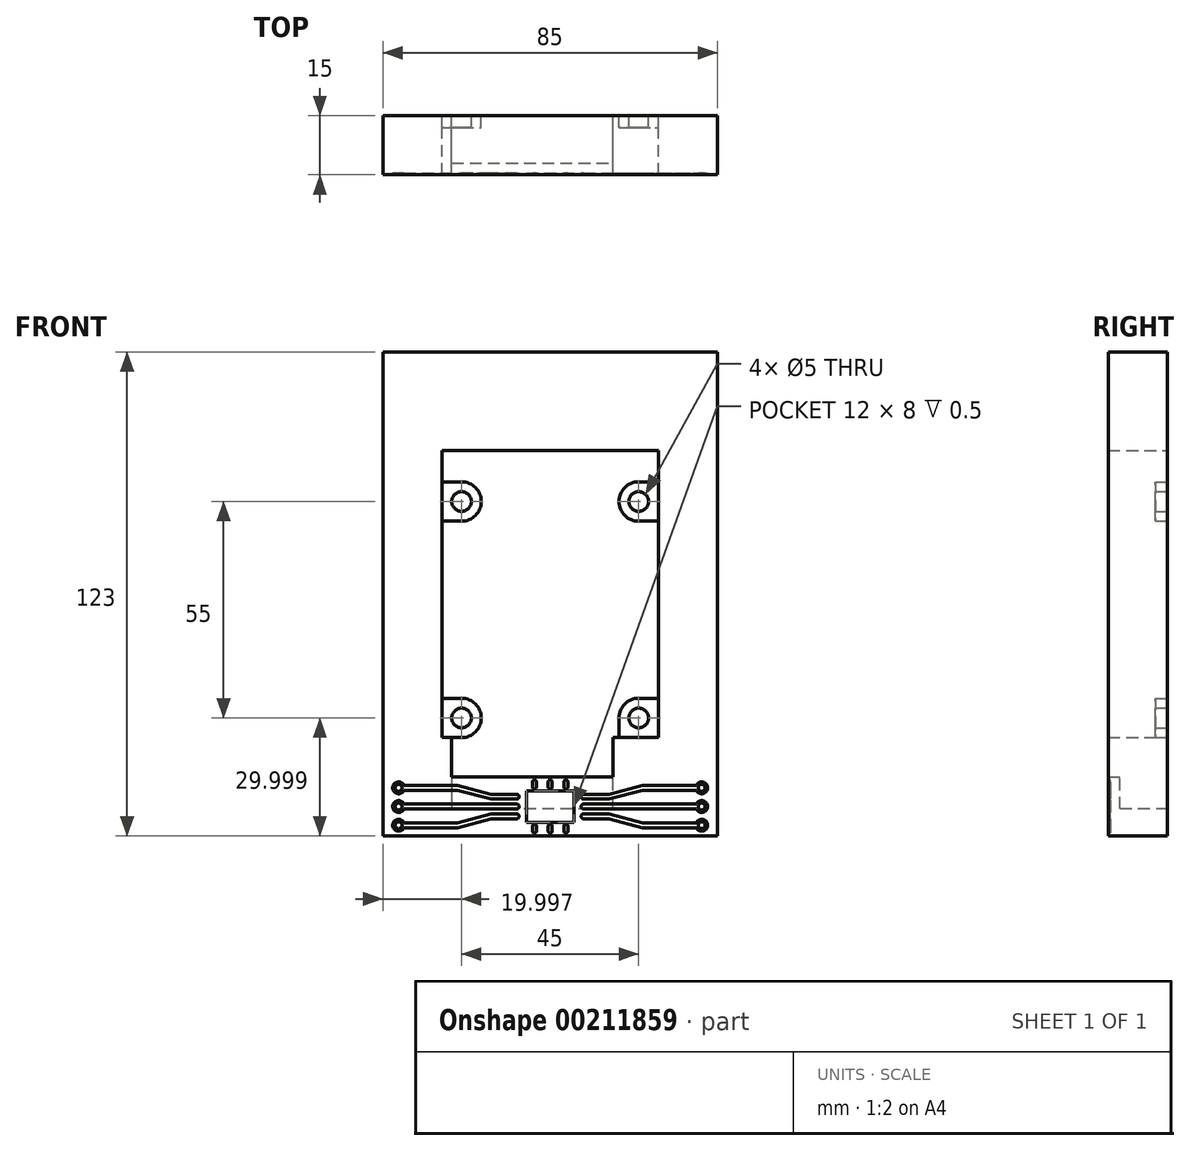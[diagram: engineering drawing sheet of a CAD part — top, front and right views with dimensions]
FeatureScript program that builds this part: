
annotation { "Feature Type Name" : "Feature", "Feature Type Description" : "" }
export const myFeature = defineFeature(function(context is Context, id is Id, definition is map)
    precondition{}
    {
        {
            var Q0;
            Q0=qCreatedBy(makeId("Front.planeOp"),FACE);
            var sketch = newSketch(context, id + "F0", { "sketchPlane" : qUnion([Q0])});
            skLineSegment(sketch, "E0.bottom", {"start": v(-49.2, 57.76) * mm, "end": v(35.8, 57.76) * mm});
            skLineSegment(sketch, "E0.top", {"start": v(-49.2, -65.24) * mm, "end": v(35.8, -65.24) * mm});
            skLineSegment(sketch, "E0.left", {"start": v(-49.2, 57.76) * mm, "end": v(-49.2, -65.24) * mm});
            skLineSegment(sketch, "E0.right", {"start": v(35.8, 57.76) * mm, "end": v(35.8, -65.24) * mm});
            skLineSegment(sketch, "E1.bottom", {"start": v(-34.2, 32.76) * mm, "end": v(20.8, 32.76) * mm});
            skLineSegment(sketch, "E1.top", {"start": v(-34.2, -40.24) * mm, "end": v(20.8, -40.24) * mm});
            skLineSegment(sketch, "E1.left", {"start": v(-34.2, 32.76) * mm, "end": v(-34.2, -40.24) * mm});
            skLineSegment(sketch, "E1.right", {"start": v(20.8, 32.76) * mm, "end": v(20.8, -40.24) * mm});
            skLineSegment(sketch, "E2", {"start": v(-34.2, 21.12) * mm, "end": v(-49.2, 21.12) * mm, "construction": true});
            skLineSegment(sketch, "E3", {"start": v(20.8, 21.67) * mm, "end": v(35.8, 21.67) * mm, "construction": true});
            skCircle(sketch, "E4", {"center": v(-29.2, 19.76) * mm, "radius": 2.5 * mm});
            skCircle(sketch, "E5", {"center": v(15.8, 19.76) * mm, "radius": 2.5 * mm});
            skCircle(sketch, "E6", {"center": v(-29.2, -35.24) * mm, "radius": 2.5 * mm});
            skCircle(sketch, "E7", {"center": v(15.8, -35.24) * mm, "radius": 2.5 * mm});
            skLineSegment(sketch, "E8", {"start": v(-41.13, 19.76) * mm, "end": v(28.25, 19.76) * mm, "construction": true});
            skLineSegment(sketch, "E9", {"start": v(25.62, -35.24) * mm, "end": v(-43.94, -35.24) * mm, "construction": true});
            skLineSegment(sketch, "E10", {"start": v(15.8, 37.64) * mm, "end": v(15.8, -42.2) * mm, "construction": true});
            skLineSegment(sketch, "E11", {"start": v(-29.2, -41.94) * mm, "end": v(-29.2, 36.03) * mm, "construction": true});
            skLineSegment(sketch, "E12", {"start": v(-34.2, 2.25) * mm, "end": v(-29.2, 2.25) * mm, "construction": true});
            skLineSegment(sketch, "E13", {"start": v(15.8, 2.62) * mm, "end": v(20.8, 2.62) * mm, "construction": true});
            skArc(sketch, "E14", {"start": v(-29.2, 14.76) * mm, "mid": v(-24.2, 19.76) * mm, "end": v(-29.2, 24.76) * mm});
            skArc(sketch, "E15", {"start": v(15.8, 24.76) * mm, "mid": v(10.8, 19.76) * mm, "end": v(15.8, 14.76) * mm});
            skArc(sketch, "E16", {"start": v(-29.2, -40.24) * mm, "mid": v(-24.2, -35.24) * mm, "end": v(-29.2, -30.24) * mm});
            skArc(sketch, "E17", {"start": v(15.8, -30.24) * mm, "mid": v(12.26, -31.7) * mm, "end": v(10.8, -35.24) * mm});
            skLineSegment(sketch, "E18", {"start": v(-34.2, 24.76) * mm, "end": v(-29.2, 24.76) * mm});
            skLineSegment(sketch, "E19", {"start": v(-29.2, 14.76) * mm, "end": v(-34.2, 14.76) * mm});
            skLineSegment(sketch, "E20", {"start": v(15.8, 24.76) * mm, "end": v(20.8, 24.76) * mm});
            skLineSegment(sketch, "E21", {"start": v(15.8, 14.76) * mm, "end": v(20.8, 14.76) * mm});
            skLineSegment(sketch, "E22", {"start": v(15.8, -30.24) * mm, "end": v(20.8, -30.24) * mm});
            skLineSegment(sketch, "E23", {"start": v(20.8, -40.24) * mm, "end": v(15.8, -40.24) * mm});
            skLineSegment(sketch, "E24", {"start": v(-29.2, -40.24) * mm, "end": v(-34.2, -40.24) * mm});
            skLineSegment(sketch, "E25", {"start": v(-29.2, -30.24) * mm, "end": v(-34.2, -30.24) * mm});
            skLineSegment(sketch, "E26", {"start": v(-31.7, -40.24) * mm, "end": v(-31.7, -58.24) * mm});
            skLineSegment(sketch, "E27", {"start": v(-31.7, -58.24) * mm, "end": v(9.3, -58.24) * mm});
            skLineSegment(sketch, "E28", {"start": v(9.3, -58.24) * mm, "end": v(9.3, -40.24) * mm});
            skLineSegment(sketch, "E29", {"start": v(10.8, -35.24) * mm, "end": v(10.8, -40.24) * mm});
            skLineSegment(sketch, "E30", {"start": v(9.3, -50.24) * mm, "end": v(-31.7, -50.24) * mm});
            skSolve(sketch);
        }
        {
            var Q0;
            Q0=makeQuery(id+"F0.imprint","IMPRINT",FACE,{"disambiguationData":[TD([[makeQuery(id+"F0.imprint","IMPRINT",EDGE,{"derivedFrom":sQuery(id+"F0.wireOp",EDGE,"E0.bottom")}),-1.0]])]});
            extrude(context, id + "F1", {"entities" : qUnion([Q0]), "depth" : 15 * mm});
        }
        {
            var Q0;
            Q0=makeQuery(id+"F0.imprint","IMPRINT",FACE,{"disambiguationData":[TD([[makeQuery(id+"F0.imprint","IMPRINT",EDGE,{"derivedFrom":sQuery(id+"F0.wireOp",EDGE,"E4")}),-1.0]])]});
            var Q1;
            Q1=makeQuery(id+"F0.imprint","IMPRINT",FACE,{"disambiguationData":[TD([[makeQuery(id+"F0.imprint","IMPRINT",EDGE,{"derivedFrom":sQuery(id+"F0.wireOp",EDGE,"E5")}),-1.0]])]});
            var Q2;
            Q2=makeQuery(id+"F0.imprint","IMPRINT",FACE,{"disambiguationData":[TD([[makeQuery(id+"F0.imprint","IMPRINT",EDGE,{"derivedFrom":sQuery(id+"F0.wireOp",EDGE,"E7")}),-1.0]])]});
            var Q3;
            Q3=makeQuery(id+"F0.imprint","IMPRINT",FACE,{"disambiguationData":[TD([[makeQuery(id+"F0.imprint","IMPRINT",EDGE,{"derivedFrom":sQuery(id+"F0.wireOp",EDGE,"E6")}),-1.0]])]});
            extrude(context, id + "F2", {"entities" : qUnion([Q0, Q1, Q2, Q3]), "operationType" : NewBodyOperationType.ADD, "depth" : 3 * mm});
        }
        {
            var Q0;
            {var subQ0=sQuery(id+"F0.wireOp",EDGE,"E27");Q0=makeQuery(id+"F0.imprint","IMPRINT",FACE,{"disambiguationData":[TD([[makeQuery(id+"F0.imprint","IMPRINT",EDGE,{"derivedFrom":subQ0}),1.0]])]});}
            extrude(context, id + "F3", {"entities" : qUnion([Q0]), "operationType" : NewBodyOperationType.ADD, "depth" : 15 * mm, "hasSecondDirection" : true, "secondDirectionOppositeDirection" : false, "secondDirectionDepth" : 12 * mm});
        }
        {
            var Q0;
            {var subQ0=sQuery(id+"F0.wireOp",EDGE,"E28");var subQ1=sQuery(id+"F0.wireOp",EDGE,"E27");var subQ2=sQuery(id+"F0.wireOp",EDGE,"E26");Q0=makeQuery(id+"F3.boolean.opBoolean","MERGE",FACE,{"derivedFrom":[makeQuery(id+"F1.opExtrude","CAP_FACE",FACE,{"disambiguationData":[OSD([sQuery(id+"F0.wireOp",EDGE,"E0.bottom"),sQuery(id+"F0.wireOp",EDGE,"E0.top"),sQuery(id+"F0.wireOp",EDGE,"E0.left"),sQuery(id+"F0.wireOp",EDGE,"E0.right"),sQuery(id+"F0.wireOp",EDGE,"E1.bottom"),sQuery(id+"F0.wireOp",EDGE,"E1.top"),sQuery(id+"F0.wireOp",EDGE,"E1.left"),sQuery(id+"F0.wireOp",EDGE,"E1.right"),sQuery(id+"F0.wireOp",EDGE,"E23"),sQuery(id+"F0.wireOp",EDGE,"E24"),subQ2,subQ1,subQ0])],"isStart":false}),makeQuery(id+"F3.opExtrude","CAP_FACE",FACE,{"disambiguationData":[OSD([subQ2,subQ1,subQ0,sQuery(id+"F0.wireOp",EDGE,"E30")])],"isStart":false})]});}
            var sketch = newSketch(context, id + "F4", { "sketchPlane" : qUnion([Q0])});
            skCircle(sketch, "E31", {"center": v(-45.2, -53) * mm, "radius": 0.88 * mm});
            skCircle(sketch, "E32", {"center": v(-45.2, -57.74) * mm, "radius": 0.88 * mm});
            skCircle(sketch, "E33", {"center": v(-45.2, -62.5) * mm, "radius": 0.88 * mm});
            skCircle(sketch, "E34", {"center": v(31.8, -53) * mm, "radius": 0.88 * mm});
            skCircle(sketch, "E35", {"center": v(31.8, -57.74) * mm, "radius": 0.88 * mm});
            skCircle(sketch, "E36", {"center": v(31.8, -62.5) * mm, "radius": 0.88 * mm});
            skArc(sketch, "E37", {"start": v(-43.84, -52.37) * mm, "mid": v(-46.7, -53) * mm, "end": v(-43.84, -53.62) * mm});
            skArc(sketch, "E38", {"start": v(-43.84, -57.12) * mm, "mid": v(-46.7, -57.74) * mm, "end": v(-43.84, -58.37) * mm});
            skArc(sketch, "E39", {"start": v(-43.84, -61.87) * mm, "mid": v(-46.7, -62.5) * mm, "end": v(-43.84, -63.12) * mm});
            skArc(sketch, "E40", {"start": v(30.43, -53.62) * mm, "mid": v(33.3, -53) * mm, "end": v(30.43, -52.37) * mm});
            skArc(sketch, "E41", {"start": v(30.43, -58.37) * mm, "mid": v(33.3, -57.74) * mm, "end": v(30.43, -57.12) * mm});
            skArc(sketch, "E42", {"start": v(30.43, -63.12) * mm, "mid": v(33.3, -62.5) * mm, "end": v(30.43, -61.87) * mm});
            skLineSegment(sketch, "E43", {"start": v(31.8, -57.74) * mm, "end": v(-45.2, -57.74) * mm, "construction": true});
            skLineSegment(sketch, "E44", {"start": v(-45.2, -62.5) * mm, "end": v(-45.2, -57.74) * mm, "construction": true});
            skLineSegment(sketch, "E45", {"start": v(-45.2, -53) * mm, "end": v(-45.2, -57.74) * mm, "construction": true});
            skLineSegment(sketch, "E46", {"start": v(31.8, -53) * mm, "end": v(31.8, -57.74) * mm, "construction": true});
            skLineSegment(sketch, "E47", {"start": v(31.8, -57.74) * mm, "end": v(31.8, -62.5) * mm, "construction": true});
            skLineSegment(sketch, "E48", {"start": v(-45.2, -62.5) * mm, "end": v(-49.2, -62.5) * mm, "construction": true});
            skLineSegment(sketch, "E49", {"start": v(31.8, -62.5) * mm, "end": v(35.8, -62.5) * mm, "construction": true});
            skLineSegment(sketch, "E50", {"start": v(-6.7, -65.24) * mm, "end": v(-6.7, -60.24) * mm, "construction": true});
            skLineSegment(sketch, "E51", {"start": v(-11.2, -50.24) * mm, "end": v(-11.2, -55.24) * mm, "construction": true});
            skLineSegment(sketch, "E52", {"start": v(-11.2, -55.24) * mm, "end": v(-11.2, -57.74) * mm, "construction": true});
            skLineSegment(sketch, "E53", {"start": v(-6.7, -60.24) * mm, "end": v(-6.7, -57.74) * mm, "construction": true});
            skLineSegment(sketch, "E54", {"start": v(-11.2, -55.24) * mm, "end": v(-21.7, -55.24) * mm, "construction": true});
            skLineSegment(sketch, "E55", {"start": v(-11.2, -55.24) * mm, "end": v(8.3, -55.24) * mm, "construction": true});
            skLineSegment(sketch, "E56", {"start": v(-6.7, -60.24) * mm, "end": v(8.3, -60.24) * mm, "construction": true});
            skLineSegment(sketch, "E57", {"start": v(-6.7, -60.24) * mm, "end": v(-21.7, -60.24) * mm, "construction": true});
            skLineSegment(sketch, "E58", {"start": v(-21.7, -55.24) * mm, "end": v(-21.7, -60.24) * mm, "construction": true});
            skLineSegment(sketch, "E59", {"start": v(8.3, -60.24) * mm, "end": v(8.3, -55.24) * mm, "construction": true});
            skLineSegment(sketch, "E60", {"start": v(-45.2, -53) * mm, "end": v(-30.2, -53) * mm, "construction": true});
            skLineSegment(sketch, "E61", {"start": v(-30.2, -53) * mm, "end": v(-21.7, -55.24) * mm, "construction": true});
            skLineSegment(sketch, "E62", {"start": v(-21.7, -60.24) * mm, "end": v(-30.2, -62.5) * mm, "construction": true});
            skLineSegment(sketch, "E63", {"start": v(-30.2, -62.5) * mm, "end": v(-45.2, -62.5) * mm, "construction": true});
            skLineSegment(sketch, "E64", {"start": v(8.3, -60.24) * mm, "end": v(16.8, -62.5) * mm, "construction": true});
            skLineSegment(sketch, "E65", {"start": v(16.8, -62.5) * mm, "end": v(31.8, -62.5) * mm, "construction": true});
            skLineSegment(sketch, "E66", {"start": v(31.8, -53) * mm, "end": v(16.8, -53) * mm, "construction": true});
            skLineSegment(sketch, "E67", {"start": v(16.8, -53) * mm, "end": v(8.3, -55.24) * mm, "construction": true});
            skLineSegment(sketch, "E68", {"start": v(-6.7, -61.74) * mm, "end": v(-0.7, -61.74) * mm});
            skLineSegment(sketch, "E69", {"start": v(-0.7, -61.74) * mm, "end": v(-0.7, -57.74) * mm});
            skLineSegment(sketch, "E70", {"start": v(-0.7, -57.74) * mm, "end": v(-0.7, -53.74) * mm});
            skLineSegment(sketch, "E71", {"start": v(-0.7, -53.74) * mm, "end": v(-6.7, -53.74) * mm});
            skLineSegment(sketch, "E72", {"start": v(-6.7, -53.74) * mm, "end": v(-6.7, -57.74) * mm, "construction": true});
            skLineSegment(sketch, "E73", {"start": v(-6.7, -53.74) * mm, "end": v(-12.7, -53.74) * mm});
            skLineSegment(sketch, "E74", {"start": v(-12.7, -53.74) * mm, "end": v(-12.7, -57.74) * mm});
            skLineSegment(sketch, "E75", {"start": v(-12.7, -57.74) * mm, "end": v(-12.7, -61.74) * mm});
            skLineSegment(sketch, "E76", {"start": v(-12.7, -61.74) * mm, "end": v(-6.7, -61.74) * mm});
            skLineSegment(sketch, "E77", {"start": v(-43.84, -52.37) * mm, "end": v(-30.2, -52.37) * mm});
            skLineSegment(sketch, "E78", {"start": v(-30.2, -52.37) * mm, "end": v(-21.7, -54.62) * mm});
            skLineSegment(sketch, "E79", {"start": v(-21.7, -54.62) * mm, "end": v(-15.2, -54.62) * mm});
            skLineSegment(sketch, "E80", {"start": v(-43.84, -53.62) * mm, "end": v(-30.2, -53.62) * mm});
            skLineSegment(sketch, "E81", {"start": v(-30.2, -53.62) * mm, "end": v(-21.7, -55.87) * mm});
            skLineSegment(sketch, "E82", {"start": v(-21.7, -55.87) * mm, "end": v(-15.2, -55.87) * mm});
            skLineSegment(sketch, "E83", {"start": v(-30.2, -53) * mm, "end": v(-30.2, -52.37) * mm, "construction": true});
            skLineSegment(sketch, "E84", {"start": v(-30.2, -53) * mm, "end": v(-30.2, -53.62) * mm, "construction": true});
            skArc(sketch, "E85", {"start": v(-15.2, -55.87) * mm, "mid": v(-14.58, -55.24) * mm, "end": v(-15.2, -54.62) * mm});
            skLineSegment(sketch, "E86", {"start": v(-21.7, -55.24) * mm, "end": v(-21.7, -54.62) * mm, "construction": true});
            skLineSegment(sketch, "E87", {"start": v(-15.2, -55.24) * mm, "end": v(-15.2, -55.87) * mm, "construction": true});
            skLineSegment(sketch, "E88", {"start": v(-15.2, -55.24) * mm, "end": v(-15.2, -54.62) * mm, "construction": true});
            skLineSegment(sketch, "E89", {"start": v(-43.84, -57.12) * mm, "end": v(-15.2, -57.12) * mm});
            skLineSegment(sketch, "E90", {"start": v(-15.2, -57.12) * mm, "end": v(-15.2, -57.74) * mm, "construction": true});
            skLineSegment(sketch, "E91", {"start": v(-15.2, -57.74) * mm, "end": v(-15.2, -58.37) * mm, "construction": true});
            skLineSegment(sketch, "E92", {"start": v(-15.2, -58.37) * mm, "end": v(-43.84, -58.37) * mm});
            skArc(sketch, "E93", {"start": v(-15.2, -58.37) * mm, "mid": v(-14.58, -57.74) * mm, "end": v(-15.2, -57.12) * mm});
            skLineSegment(sketch, "E94", {"start": v(-15.2, -55.87) * mm, "end": v(-15.2, -57.12) * mm, "construction": true});
            skLineSegment(sketch, "E95", {"start": v(-43.84, -61.87) * mm, "end": v(-30.2, -61.87) * mm});
            skLineSegment(sketch, "E96", {"start": v(-30.2, -61.87) * mm, "end": v(-21.7, -59.62) * mm});
            skLineSegment(sketch, "E97", {"start": v(-21.7, -59.62) * mm, "end": v(-15.2, -59.62) * mm});
            skLineSegment(sketch, "E98", {"start": v(-15.2, -59.62) * mm, "end": v(-15.2, -60.24) * mm, "construction": true});
            skLineSegment(sketch, "E99", {"start": v(-15.2, -60.24) * mm, "end": v(-15.2, -60.87) * mm, "construction": true});
            skLineSegment(sketch, "E100", {"start": v(-15.2, -60.87) * mm, "end": v(-21.7, -60.87) * mm});
            skLineSegment(sketch, "E101", {"start": v(-21.7, -60.87) * mm, "end": v(-30.2, -63.12) * mm});
            skLineSegment(sketch, "E102", {"start": v(-30.2, -63.12) * mm, "end": v(-43.84, -63.12) * mm});
            skLineSegment(sketch, "E103", {"start": v(-30.2, -62.5) * mm, "end": v(-30.2, -61.87) * mm, "construction": true});
            skLineSegment(sketch, "E104", {"start": v(-30.2, -63.12) * mm, "end": v(-30.2, -62.5) * mm, "construction": true});
            skLineSegment(sketch, "E105", {"start": v(-21.7, -60.24) * mm, "end": v(-21.7, -60.87) * mm, "construction": true});
            skLineSegment(sketch, "E106", {"start": v(-15.2, -59.62) * mm, "end": v(-15.2, -58.37) * mm, "construction": true});
            skArc(sketch, "E107", {"start": v(-15.2, -60.87) * mm, "mid": v(-14.58, -60.24) * mm, "end": v(-15.2, -59.62) * mm});
            skLineSegment(sketch, "E108", {"start": v(30.43, -52.37) * mm, "end": v(16.8, -52.37) * mm});
            skLineSegment(sketch, "E109", {"start": v(16.8, -52.37) * mm, "end": v(8.3, -54.62) * mm});
            skLineSegment(sketch, "E110", {"start": v(8.3, -54.62) * mm, "end": v(1.8, -54.62) * mm});
            skLineSegment(sketch, "E111", {"start": v(1.8, -54.62) * mm, "end": v(1.8, -55.24) * mm, "construction": true});
            skLineSegment(sketch, "E112", {"start": v(1.8, -55.24) * mm, "end": v(1.8, -55.87) * mm, "construction": true});
            skLineSegment(sketch, "E113", {"start": v(1.8, -55.87) * mm, "end": v(8.3, -55.87) * mm});
            skLineSegment(sketch, "E114", {"start": v(8.3, -55.87) * mm, "end": v(16.8, -53.62) * mm});
            skLineSegment(sketch, "E115", {"start": v(16.8, -53.62) * mm, "end": v(30.43, -53.62) * mm});
            skLineSegment(sketch, "E116", {"start": v(16.8, -52.37) * mm, "end": v(16.8, -53) * mm, "construction": true});
            skLineSegment(sketch, "E117", {"start": v(16.8, -53.62) * mm, "end": v(16.8, -53) * mm, "construction": true});
            skLineSegment(sketch, "E118", {"start": v(8.3, -54.62) * mm, "end": v(8.3, -55.24) * mm, "construction": true});
            skArc(sketch, "E119", {"start": v(1.8, -54.62) * mm, "mid": v(1.17, -55.24) * mm, "end": v(1.8, -55.87) * mm});
            skLineSegment(sketch, "E120", {"start": v(1.8, -54.62) * mm, "end": v(-0.7, -54.62) * mm, "construction": true});
            skLineSegment(sketch, "E121", {"start": v(-15.2, -54.62) * mm, "end": v(-12.7, -54.62) * mm, "construction": true});
            skLineSegment(sketch, "E122", {"start": v(30.43, -57.12) * mm, "end": v(1.8, -57.12) * mm});
            skLineSegment(sketch, "E123", {"start": v(1.8, -58.37) * mm, "end": v(30.43, -58.37) * mm});
            skLineSegment(sketch, "E124", {"start": v(1.8, -57.74) * mm, "end": v(1.8, -58.37) * mm, "construction": true});
            skLineSegment(sketch, "E125", {"start": v(1.8, -57.12) * mm, "end": v(1.8, -57.74) * mm, "construction": true});
            skArc(sketch, "E126", {"start": v(1.8, -57.12) * mm, "mid": v(1.17, -57.74) * mm, "end": v(1.8, -58.37) * mm});
            skLineSegment(sketch, "E127", {"start": v(1.8, -55.87) * mm, "end": v(1.8, -57.12) * mm, "construction": true});
            skLineSegment(sketch, "E128", {"start": v(30.43, -61.87) * mm, "end": v(16.8, -61.87) * mm});
            skLineSegment(sketch, "E129", {"start": v(16.8, -61.87) * mm, "end": v(16.8, -62.5) * mm, "construction": true});
            skLineSegment(sketch, "E130", {"start": v(16.8, -61.87) * mm, "end": v(8.3, -59.62) * mm});
            skLineSegment(sketch, "E131", {"start": v(8.3, -60.24) * mm, "end": v(8.3, -60.87) * mm, "construction": true});
            skLineSegment(sketch, "E132", {"start": v(8.3, -60.87) * mm, "end": v(16.8, -63.12) * mm});
            skLineSegment(sketch, "E133", {"start": v(16.8, -63.12) * mm, "end": v(16.8, -62.5) * mm, "construction": true});
            skLineSegment(sketch, "E134", {"start": v(16.8, -63.12) * mm, "end": v(30.43, -63.12) * mm});
            skLineSegment(sketch, "E135", {"start": v(8.3, -59.62) * mm, "end": v(1.8, -59.62) * mm});
            skLineSegment(sketch, "E136", {"start": v(1.8, -59.62) * mm, "end": v(1.8, -60.24) * mm, "construction": true});
            skLineSegment(sketch, "E137", {"start": v(1.8, -60.24) * mm, "end": v(1.8, -60.87) * mm, "construction": true});
            skLineSegment(sketch, "E138", {"start": v(1.8, -60.87) * mm, "end": v(8.3, -60.87) * mm});
            skLineSegment(sketch, "E139", {"start": v(1.8, -58.37) * mm, "end": v(1.8, -59.62) * mm, "construction": true});
            skArc(sketch, "E140", {"start": v(1.8, -59.62) * mm, "mid": v(1.17, -60.24) * mm, "end": v(1.8, -60.87) * mm});
            skArc(sketch, "E141", {"start": v(-6.2, -51.5) * mm, "mid": v(-6.7, -51) * mm, "end": v(-7.2, -51.5) * mm});
            skArc(sketch, "E142", {"start": v(-7.2, -52.74) * mm, "mid": v(-6.7, -53.24) * mm, "end": v(-6.2, -52.74) * mm});
            skLineSegment(sketch, "E143", {"start": v(-6.2, -52.74) * mm, "end": v(-6.2, -51.5) * mm});
            skLineSegment(sketch, "E144", {"start": v(-7.2, -51.5) * mm, "end": v(-7.2, -52.74) * mm});
            skLineSegment(sketch, "E145", {"start": v(-6.7, -52.74) * mm, "end": v(-6.7, -53.74) * mm, "construction": true});
            skLineSegment(sketch, "E146", {"start": v(-6.7, -52.74) * mm, "end": v(-6.7, -51.5) * mm, "construction": true});
            skArc(sketch, "E147", {"start": v(-2.2, -51.5) * mm, "mid": v(-2.7, -51) * mm, "end": v(-3.2, -51.5) * mm});
            skArc(sketch, "E148", {"start": v(-3.2, -52.74) * mm, "mid": v(-2.7, -53.24) * mm, "end": v(-2.2, -52.74) * mm});
            skLineSegment(sketch, "E149", {"start": v(-2.2, -51.5) * mm, "end": v(-2.2, -52.74) * mm});
            skLineSegment(sketch, "E150", {"start": v(-3.2, -51.5) * mm, "end": v(-3.2, -52.74) * mm});
            skLineSegment(sketch, "E151", {"start": v(-2.7, -52.74) * mm, "end": v(-2.7, -53.74) * mm, "construction": true});
            skLineSegment(sketch, "E152", {"start": v(-2.7, -52.74) * mm, "end": v(-2.7, -51.5) * mm, "construction": true});
            skLineSegment(sketch, "E153", {"start": v(-6.7, -52.74) * mm, "end": v(-2.7, -52.74) * mm, "construction": true});
            skLineSegment(sketch, "E154", {"start": v(-6.7, -52.74) * mm, "end": v(-7.2, -52.74) * mm, "construction": true});
            skLineSegment(sketch, "E155", {"start": v(-2.7, -52.74) * mm, "end": v(-2.2, -52.74) * mm, "construction": true});
            skLineSegment(sketch, "E156", {"start": v(-7.2, -52.74) * mm, "end": v(-10.2, -52.74) * mm, "construction": true});
            skLineSegment(sketch, "E157", {"start": v(-10.2, -52.74) * mm, "end": v(-10.2, -51.5) * mm});
            skLineSegment(sketch, "E158", {"start": v(-11.2, -51.5) * mm, "end": v(-11.2, -52.74) * mm});
            skArc(sketch, "E159", {"start": v(-10.2, -51.5) * mm, "mid": v(-10.7, -51) * mm, "end": v(-11.2, -51.5) * mm});
            skArc(sketch, "E160", {"start": v(-11.2, -52.74) * mm, "mid": v(-10.7, -53.24) * mm, "end": v(-10.2, -52.74) * mm});
            skLineSegment(sketch, "E161", {"start": v(-10.7, -52.74) * mm, "end": v(-10.7, -53.74) * mm, "construction": true});
            skLineSegment(sketch, "E162", {"start": v(-10.7, -52.74) * mm, "end": v(-10.7, -51.5) * mm, "construction": true});
            skLineSegment(sketch, "E163", {"start": v(-10.2, -52.74) * mm, "end": v(-10.7, -52.74) * mm, "construction": true});
            skLineSegment(sketch, "E164", {"start": v(-6.2, -51.5) * mm, "end": v(-3.2, -51.5) * mm, "construction": true});
            skLineSegment(sketch, "E165", {"start": v(-2.7, -61.74) * mm, "end": v(-2.7, -62.74) * mm, "construction": true});
            skLineSegment(sketch, "E166", {"start": v(-2.7, -62.74) * mm, "end": v(-2.7, -64) * mm, "construction": true});
            skLineSegment(sketch, "E167", {"start": v(-10.7, -61.74) * mm, "end": v(-10.7, -62.74) * mm, "construction": true});
            skLineSegment(sketch, "E168", {"start": v(-10.7, -62.74) * mm, "end": v(-10.7, -64) * mm, "construction": true});
            skArc(sketch, "E169", {"start": v(-11.2, -64) * mm, "mid": v(-10.7, -64.5) * mm, "end": v(-10.2, -64) * mm});
            skArc(sketch, "E170", {"start": v(-10.2, -62.74) * mm, "mid": v(-10.7, -62.24) * mm, "end": v(-11.2, -62.74) * mm});
            skArc(sketch, "E171", {"start": v(-3.2, -64) * mm, "mid": v(-2.7, -64.5) * mm, "end": v(-2.2, -64) * mm});
            skArc(sketch, "E172", {"start": v(-2.2, -62.74) * mm, "mid": v(-2.7, -62.24) * mm, "end": v(-3.2, -62.74) * mm});
            skLineSegment(sketch, "E173", {"start": v(-2.2, -62.74) * mm, "end": v(-2.2, -64) * mm});
            skLineSegment(sketch, "E174", {"start": v(-3.2, -64) * mm, "end": v(-3.2, -62.74) * mm});
            skLineSegment(sketch, "E175", {"start": v(-10.2, -62.74) * mm, "end": v(-10.2, -64) * mm});
            skLineSegment(sketch, "E176", {"start": v(-11.2, -62.74) * mm, "end": v(-11.2, -64) * mm});
            skLineSegment(sketch, "E177", {"start": v(-7.2, -62.74) * mm, "end": v(-7.2, -64) * mm});
            skLineSegment(sketch, "E178", {"start": v(-6.2, -62.74) * mm, "end": v(-6.2, -64) * mm});
            skArc(sketch, "E179", {"start": v(-6.2, -62.74) * mm, "mid": v(-6.7, -62.24) * mm, "end": v(-7.2, -62.74) * mm});
            skArc(sketch, "E180", {"start": v(-7.2, -64) * mm, "mid": v(-6.7, -64.5) * mm, "end": v(-6.2, -64) * mm});
            skLineSegment(sketch, "E181", {"start": v(-6.2, -62.74) * mm, "end": v(-3.2, -62.74) * mm, "construction": true});
            skLineSegment(sketch, "E182", {"start": v(-7.2, -62.74) * mm, "end": v(-10.2, -62.74) * mm, "construction": true});
            skLineSegment(sketch, "E183", {"start": v(-10.2, -62.74) * mm, "end": v(-10.7, -62.74) * mm, "construction": true});
            skLineSegment(sketch, "E184", {"start": v(-7.2, -62.74) * mm, "end": v(-6.7, -62.74) * mm, "construction": true});
            skLineSegment(sketch, "E185", {"start": v(-3.2, -62.74) * mm, "end": v(-2.7, -62.74) * mm, "construction": true});
            skSolve(sketch);
        }
        {
            var Q0;
            Q0 = qSketchRegion(id + "F4", true);
            extrude(context, id + "F5", {"entities" : qUnion([Q0]), "operationType" : NewBodyOperationType.REMOVE, "oppositeDirection" : true, "depth" : .5 * mm, "offsetDistance" : 25 * mm});
        }
    });
